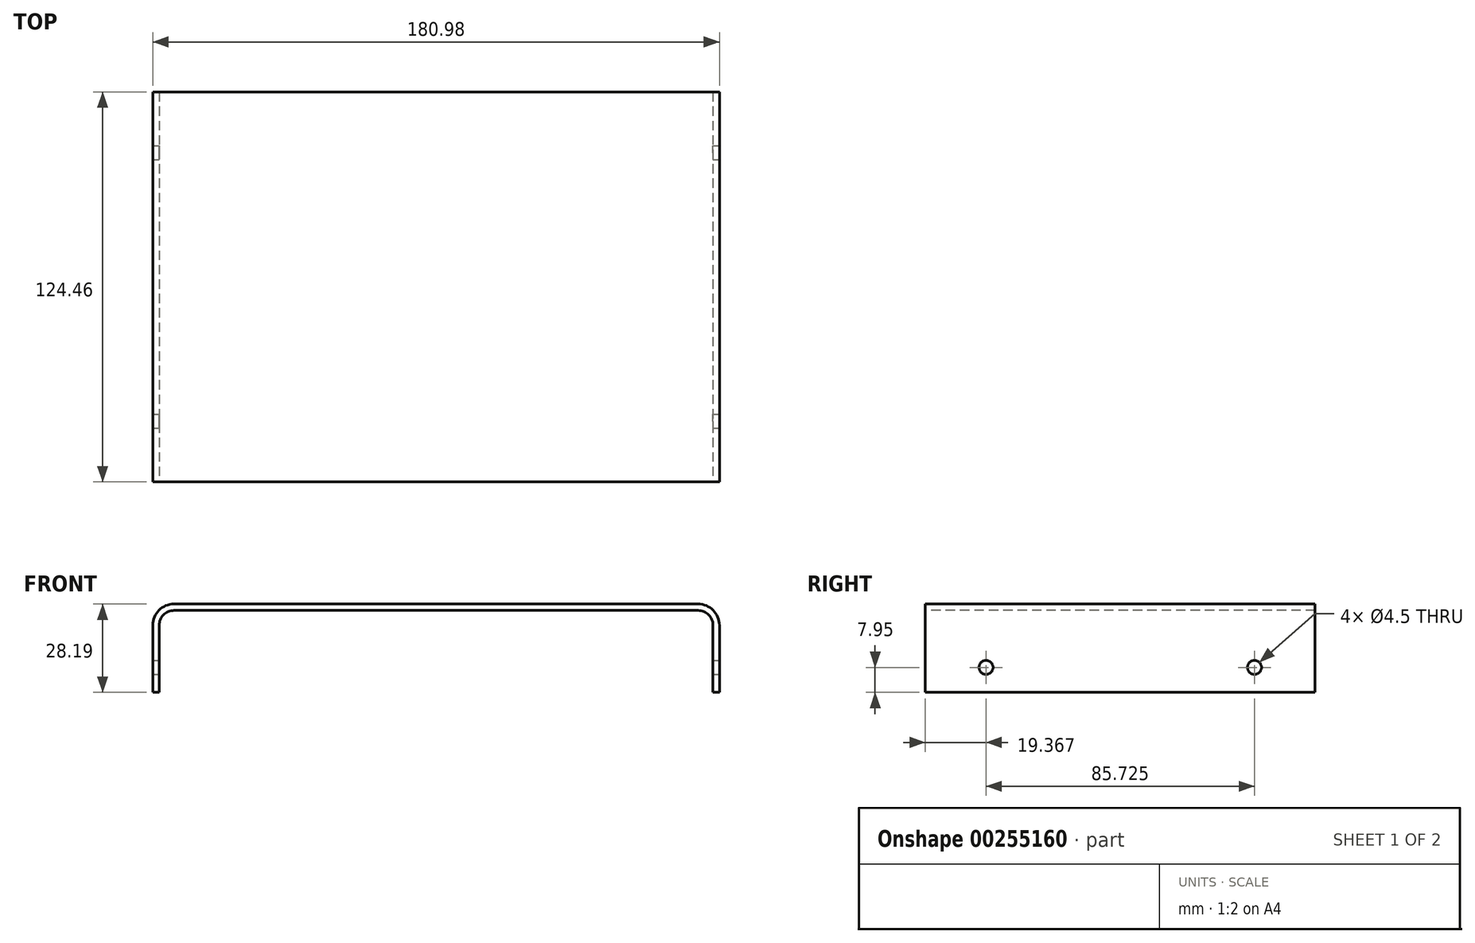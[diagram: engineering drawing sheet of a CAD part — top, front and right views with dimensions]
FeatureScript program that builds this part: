
annotation { "Feature Type Name" : "Feature", "Feature Type Description" : "" }
export const myFeature = defineFeature(function(context is Context, id is Id, definition is map)
    precondition{}
    {
        {
            var Q0;
            Q0=qCreatedBy(makeId("Front.planeOp"),FACE);
            var sketch = newSketch(context, id + "F0", { "sketchPlane" : qUnion([Q0])});
            skLineSegment(sketch, "E0", {"start": v(0, 0) * mm, "end": v(0, 21.36) * mm});
            skLineSegment(sketch, "E1", {"start": v(6.83, 28.2) * mm, "end": v(174.14, 28.2) * mm});
            skLineSegment(sketch, "E2", {"start": v(180.97, 21.36) * mm, "end": v(180.97, 0) * mm});
            skPoint(sketch, "E3.visualSharp", {"position": v(0, 28.2) * mm});
            skArc(sketch, "E3.filletArc", {"start": v(6.83, 28.2) * mm, "mid": v(2, 26.2) * mm, "end": v(0, 21.36) * mm});
            skPoint(sketch, "E4.visualSharp", {"position": v(180.98, 28.2) * mm});
            skArc(sketch, "E4.filletArc", {"start": v(180.97, 21.36) * mm, "mid": v(178.97, 26.2) * mm, "end": v(174.14, 28.2) * mm});
            skLineSegment(sketch, "E5.0", {"start": v(178.92, 21.36) * mm, "end": v(178.92, 0) * mm});
            skLineSegment(sketch, "E5.1", {"start": v(2.06, 0) * mm, "end": v(2.06, 21.36) * mm});
            skArc(sketch, "E5.2", {"start": v(6.83, 26.14) * mm, "mid": v(3.46, 24.74) * mm, "end": v(2.06, 21.36) * mm});
            skLineSegment(sketch, "E5.3", {"start": v(6.83, 26.14) * mm, "end": v(174.14, 26.14) * mm});
            skArc(sketch, "E5.4", {"start": v(178.92, 21.36) * mm, "mid": v(177.52, 24.74) * mm, "end": v(174.14, 26.14) * mm});
            skLineSegment(sketch, "E6", {"start": v(2.06, 0) * mm, "end": v(0, 0) * mm});
            skLineSegment(sketch, "E7", {"start": v(180.97, 0) * mm, "end": v(178.92, 0) * mm});
            skSolve(sketch);
        }
        {
            var Q0;
            Q0=makeQuery(id+"F0.imprint","IMPRINT",FACE,{"disambiguationData":[TD([[makeQuery(id+"F0.imprint","IMPRINT",EDGE,{"derivedFrom":sQuery(id+"F0.wireOp",EDGE,"E0")}),-1.0]])]});
            extrude(context, id + "F1", {"entities" : qUnion([Q0]), "oppositeDirection" : true, "depth" : 124.46 * mm});
        }
        {
            var Q0;
            Q0=makeQuery(id+"F1.opExtrude","SWEPT_FACE",FACE,{"disambiguationData":[OSD([sQuery(id+"F0.wireOp",EDGE,"E2")])]});
            var sketch = newSketch(context, id + "F2", { "sketchPlane" : qUnion([Q0])});
            skPoint(sketch, "E8", {"position": v(19.37, 7.95) * mm});
            skPoint(sketch, "E9", {"position": v(105.1, 7.95) * mm});
            skSolve(sketch);
        }
        {
            var Q0;
            Q0=sQuery(id+"F2.wireOp",VERTEX,"E8");
            var Q1;
            Q1=sQuery(id+"F2.wireOp",VERTEX,"E9");
            var Q2;
            Q2=makeQuery(id+"F1.opExtrude","SWEPT_BODY",BODY,{"disambiguationData":[OSD([sQuery(id+"F0.wireOp",EDGE,"E0"),sQuery(id+"F0.wireOp",EDGE,"E1"),sQuery(id+"F0.wireOp",EDGE,"E2"),sQuery(id+"F0.wireOp",EDGE,"E3.filletArc"),sQuery(id+"F0.wireOp",EDGE,"E4.filletArc"),sQuery(id+"F0.wireOp",EDGE,"E5.0"),sQuery(id+"F0.wireOp",EDGE,"E5.1"),sQuery(id+"F0.wireOp",EDGE,"E5.2"),sQuery(id+"F0.wireOp",EDGE,"E5.3"),sQuery(id+"F0.wireOp",EDGE,"E5.4"),sQuery(id+"F0.wireOp",EDGE,"E6"),sQuery(id+"F0.wireOp",EDGE,"E7")])]});
            hole(context, id + "F3", {"style" : HoleStyle.SIMPLE, "endStyle" : HoleEndStyle.THROUGH, "holeDiameter" : 4.5 * mm, "tappedDepth" : 12.7 * mm, "tapClearance" : 3, "locations" : qUnion([Q0, Q1]), "scope" : qUnion([Q2])});
        }
    });
